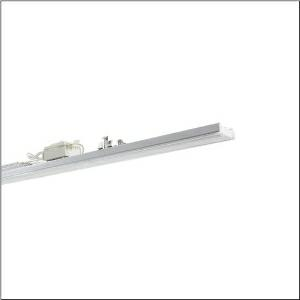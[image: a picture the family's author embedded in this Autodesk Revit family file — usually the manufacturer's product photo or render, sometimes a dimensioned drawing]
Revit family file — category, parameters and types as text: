
# Revit family: licross_21_recessed_mo_52te10dn4axg
name_source: partatom
category: Lighting Fixtures
units: mm (PartAtom-declared; Revit-internal decimal feet)

## family parameters
Cut with Voids When Loaded = No
Host = Face
Light Source = No
Part Type = Normal
Room Calculation Point = No
Round Connector Dimension = Use Diameter
Shared = No

## types (1)
- --- (1 x LED, 10000 lm, 58 W, 4000K)
    Apparent Load = 58 VA
    CIE Flux Codes = 50 81 96 100 100
    Color Rendering = 80
    Color Temperature = 4000K
    Default Elevation = 1800 mm
    Description = Licross 21 Recessed MO, luminaire insert, of sheet steel, galvanised, coil coated, white, length: 1.500mm, width: 66mm, height: 67mm, LED rated luminous flux: 10.000lm, light colour: 840, SDCM (Standard Deviation of Colour Matching)MacAdam ≤ 3 SDCM (initial), control gear: DALI 2, with plug, 5-pole, with phase selection, mains connection: 220..240V, AC, 50/60Hz, rated input power: 58W, internal wiring halogen-free, primary optical cover: cover, of PMMA, light emission: direct distribution, primary light characteristic: symmetric, protection rating (complete): IP54, insulation class (complete): insulation class I (protective earthing), certification: CE, ENEC, VDE, UKCA, protection symbol: D if used in an environment with non-conductive dust loads with corresponding accessories, impact resistance: IK06, permissible ambient temperature for indoor applications: -25..+35°C, corresponds to IFS (International Featured Standards) requirements for safety and quality in the food industry, reducing of maximum allowable ambient temperature of 5°C with ceiling mounting, LABS conformity tested according to VDMA 24364:2018-05, The light source and the operating device comply with the requirements of the Ecodesign Regulation (EU) 2019/2020 and are replaceable in accordance with this regulation, packaging unit: 1 piece
    Height = 58 mm
    Lamp = 1 x LED
    Lamp Light Flux = 10000 lm
    Lamp Power = 58 W
    Lamp count = 1
    Length = 1500 mm
    Luminous efficacy = 172 lm/W
    Manufacturer = Siteco
    ModVariant = No
    Model = 52TE10DN4AXG
    Mounting Place = Ceiling
    Mounting Type = Pendant
    Number of Poles = 1
    OnlyDefault = Yes
    Power Factor = 1
    Product Name = Licross 21 Recessed MO
    Product group = luminaire insert | ceiling pendant
    ProductGroupID = 901
    Protection Class = Protection class I
    Protection Degree = IP 54
    RLX_Detail_Level = 1
    RLX_Emergency_Light_Flux = 0 lm
    RLX_Emergency_Type = 0
    RLX_Emergency_Type_DB = No
    RlxData = <blob elided: 24693 chars, md5=e8bfba16>
    Socket = socket
    Standby Power = 0 W
    System Light Flux = 10000 lm
    System Power = 58 W
    Type Comments = factory setting: luminous flux: 100 % | dim-lin: 254 | 390 mA
    Type Image = l_1296930.jpg
    URL = http://relux.com
    VarID = @adj_127675
    Voltage = 0 V
    Weight = 0.00 kg
    Width = 66 mm

## geometry (parser evidence)
native form markers: Blend x4, Sweep x11
no freeform markers — native parametric forms only
